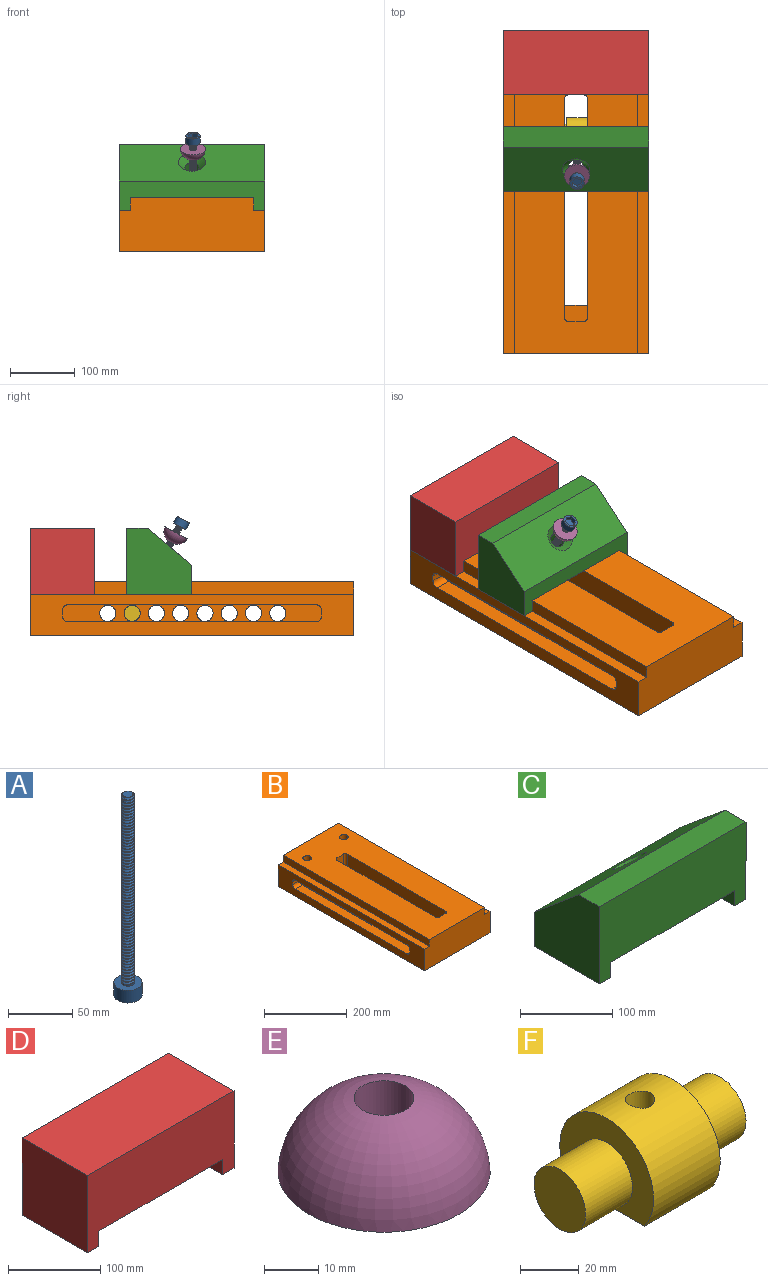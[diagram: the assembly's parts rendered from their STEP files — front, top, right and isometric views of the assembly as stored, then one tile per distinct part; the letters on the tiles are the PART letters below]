
ASSEMBLY  parts=6 mates=5
PART A: 17 faces, bbox 22x22x193.4 mm
  f0: cylinder r=5.25mm len=179mm, axis (0,0,-1), area -432.2mm2, adj f2,f5,f13,f15,f16
  f1: plane 8.52x8.52mm, normal (0,0,1), area 56mm2, adj f2,f14,f15,f16
  f2: cone r=4.25mm half-angle=45deg, axis (0,0,-1), area 19.5mm2, adj f0,f1,f14,f15
  f3: plane 22x22mm, normal (0,0,-1), area 184.4mm2, adj f4,f6,f7,f8,f9,f10,f11
  f4: cylinder r=11mm len=22mm, axis (0,0,1), area 829.4mm2, adj f3,f5
  f5: plane 22x22mm, normal (0,0,1), area 293.5mm2, adj f0,f4
  f6: plane 8.68x8mm, normal (0,1,0), area 69.4mm2, adj f3,f7,f11,f12
  f7: plane 8x7.52mm, normal (0.87,0.5,0), area 69.4mm2, adj f3,f6,f8,f12
  f8: plane 8x7.52mm, normal (0.87,-0.5,0), area 69.4mm2, adj f3,f7,f9,f12
  f9: plane 8.68x8mm, normal (0,-1,0), area 69.4mm2, adj f3,f8,f10,f12
  f10: plane 8x7.52mm, normal (-0.87,-0.5,0), area 69.4mm2, adj f3,f9,f11,f12
  f11: plane 8x7.52mm, normal (-0.87,0.5,0), area 69.4mm2, adj f3,f6,f10,f12
  f12: plane 17.36x15.04mm, normal (0,0,-1), area 195.8mm2, adj f6,f7,f8,f9,f10,f11
  f13: plane 2.39x1.3mm, normal (0,1,0.08), area 1.6mm2, adj f0,f15,f16
  f14: plane 1.1x1.01mm, normal (0,-1,-0.08), area 0mm2, adj f1,f2,f16
  f15: bspline ~180.19x12.12mm, area 3301.9mm2, adj f0,f1,f2,f13,f16
  f16: bspline ~180.2x12.12mm, area 3336.6mm2, adj f0,f1,f13,f14,f15
PART B: 84 faces, bbox 225x500x83.9 mm
  f0: plane 22.5x12.64mm, normal (0,0,-1), area 284.3mm2, adj f31,f40,f81,f83
  f1: plane 22.5x12.64mm, normal (0,0,-1), area 284.3mm2, adj f27,f36,f80,f82
  f2: plane 80x32.57mm, normal (0,0,-1), area 2340.6mm2, adj f27,f31,f32,f33,f34,f36,f37,f38
  f3: plane 22.5x12.64mm, normal (0,0,-1), area 284.3mm2, adj f31,f40,f79,f81
  f4: plane 22.5x12.64mm, normal (0,0,-1), area 284.3mm2, adj f27,f36,f78,f80
  f5: plane 22.5x12.64mm, normal (0,0,-1), area 284.3mm2, adj f31,f40,f77,f79
  f6: plane 22.5x12.64mm, normal (0,0,-1), area 284.3mm2, adj f27,f36,f76,f78
  f7: plane 22.5x12.64mm, normal (0,0,-1), area 284.3mm2, adj f31,f40,f75,f77
  f8: plane 22.5x12.64mm, normal (0,0,-1), area 284.3mm2, adj f27,f36,f74,f76
  f9: plane 22.5x12.64mm, normal (0,0,-1), area 284.3mm2, adj f31,f40,f73,f75
  f10: plane 22.5x12.64mm, normal (0,0,-1), area 284.3mm2, adj f27,f36,f72,f74
  f11: plane 22.5x12.64mm, normal (0,0,-1), area 284.3mm2, adj f31,f40,f71,f73
  f12: plane 22.5x12.64mm, normal (0,0,-1), area 284.3mm2, adj f27,f36,f70,f72
  f13: plane 22.5x12.64mm, normal (0,0,-1), area 284.3mm2, adj f31,f40,f69,f71
  f14: plane 22.5x12.64mm, normal (0,0,-1), area 284.3mm2, adj f27,f36,f68,f70
  f15: plane 30.08x22.5mm, normal (0,0,-1), area 669.1mm2, adj f29,f30,f31,f40,f69
  f16: plane 30.08x22.5mm, normal (0,0,-1), area 669.1mm2, adj f27,f28,f29,f36,f68
  f17: plane 500x225mm, normal (0,0,-1), area 83000.9mm2, adj f18,f19,f25,f26,f27,f28,f29,f30
  f18: plane 500x63.9mm, normal (-1,0,0), area 21459.5mm2, adj f17,f24,f25,f26,f47,f48,f49,f50
  f19: plane 500x63.9mm, normal (1,0,0), area 21459.5mm2, adj f17,f20,f25,f26,f59,f60,f61,f62
  f20: plane 500x17.5mm, normal (0,0,1), area 8750mm2, adj f19,f21,f25,f26
  f21: plane 500x20mm, normal (1,0,0), area 10000mm2, adj f20,f22,f25,f26
  f22: plane 500x190mm, normal (0,0,1), area 82094.8mm2, adj f21,f23,f25,f26,f36,f37,f38,f39
  f23: plane 500x20mm, normal (-1,0,0), area 10000mm2, adj f22,f24,f25,f26
  f24: plane 500x17.5mm, normal (0,0,1), area 8750mm2, adj f18,f23,f25,f26
  f25: plane 225x83.9mm, normal (0,-1,0), area 18177.5mm2, adj f17,f18,f19,f20,f21,f22,f23,f24
  f26: plane 225x83.9mm, normal (0,1,0), area 18177.5mm2, adj f17,f18,f19,f20,f21,f22,f23,f24
  f27: plane 338.01x36mm, normal (-1,0,0), area 9945.4mm2, adj f1,f2,f4,f6,f8,f10,f12,f14
  f28: cylinder r=6mm len=36mm, axis (0,0,-1), area 339.3mm2, adj f16,f17,f27,f29
  f29: plane 68x36mm, normal (0,1,0), area 2448mm2, adj f15,f16,f17,f28,f30,f35
  f30: cylinder r=6mm len=36mm, axis (0,0,-1), area 339.3mm2, adj f15,f17,f29,f31
  f31: plane 338.01x36mm, normal (1,0,0), area 9945.4mm2, adj f0,f2,f3,f5,f7,f9,f11,f13
  f32: cylinder r=6mm len=36mm, axis (0,0,-1), area 339.3mm2, adj f2,f17,f31,f33
  f33: plane 68x36mm, normal (0,-1,0), area 2448mm2, adj f2,f17,f32,f34
  f34: cylinder r=6mm len=36mm, axis (0,0,-1), area 339.3mm2, adj f2,f17,f27,f33
  f35: plane 35x24.99mm, normal (0,0,1), area 859.2mm2, adj f29,f36,f40,f41,f42,f43
  f36: plane 338x47.9mm, normal (-1,0,0), area 14486.2mm2, adj f1,f2,f4,f6,f8,f10,f12,f14
  f37: cylinder r=6mm len=47.9mm, axis (0,0,1), area 451.4mm2, adj f2,f22,f36,f38
  f38: plane 47.9x23mm, normal (0,-1,0), area 1101.7mm2, adj f2,f22,f37,f39
  f39: cylinder r=6mm len=47.9mm, axis (0,0,1), area 451.4mm2, adj f2,f22,f38,f40
  f40: plane 338x47.9mm, normal (1,0,0), area 14486.2mm2, adj f0,f2,f3,f5,f7,f9,f11,f13
  f41: cylinder r=6mm len=47.9mm, axis (0,0,1), area 451.4mm2, adj f22,f35,f40,f42
  f42: plane 47.9x23mm, normal (0,1,0), area 1101.7mm2, adj f22,f35,f41,f43
  f43: cylinder r=6mm len=47.9mm, axis (0,0,1), area 451.4mm2, adj f22,f35,f36,f42
  f44: cylinder r=10.45mm len=62.9mm, axis (0,0,-1), area 4130mm2, adj f22,f45
  f45: plane 31.2x31.2mm, normal (0,0,-1), area 421.5mm2, adj f44,f46
  f46: cylinder r=15.6mm len=31.2mm, axis (0,0,-1), area 2058.4mm2, adj f17,f45
  f47: plane 25x8.4mm, normal (0,1,0), area 210mm2, adj f18,f48,f54,f55
  f48: cylinder r=9mm len=25mm, axis (-1,0,0), area 353.4mm2, adj f18,f47,f49,f55
  f49: plane 382x25mm, normal (0,0,-1), area 9550mm2, adj f18,f48,f50,f55
  f50: cylinder r=9mm len=25mm, axis (-1,0,0), area 353.4mm2, adj f18,f49,f51,f55
  f51: plane 25x8.4mm, normal (0,-1,0), area 210mm2, adj f18,f50,f52,f55
  f52: cylinder r=9mm len=25mm, axis (-1,0,0), area 353.4mm2, adj f18,f51,f53,f55
  f53: plane 382x25mm, normal (0,0,1), area 9550mm2, adj f18,f52,f54,f55
  f54: cylinder r=9mm len=25mm, axis (-1,0,0), area 353.4mm2, adj f18,f47,f53,f55
  f55: plane 400x26.4mm, normal (-1,0,0), area 6563.5mm2, adj f47,f48,f49,f50,f51,f52,f53,f54
  f56: cylinder r=15.6mm len=31.2mm, axis (0,0,-1), area 2058.4mm2, adj f17,f57
  f57: plane 31.2x31.2mm, normal (0,0,-1), area 421.5mm2, adj f56,f58
  f58: cylinder r=10.45mm len=62.9mm, axis (0,0,-1), area 4130mm2, adj f22,f57
  f59: plane 25x8.4mm, normal (0,1,0), area 210mm2, adj f19,f60,f66,f67
  f60: cylinder r=9mm len=25mm, axis (1,0,0), area 353.4mm2, adj f19,f59,f61,f67
  f61: plane 382x25mm, normal (0,0,-1), area 9550mm2, adj f19,f60,f62,f67
  f62: cylinder r=9mm len=25mm, axis (1,0,0), area 353.4mm2, adj f19,f61,f63,f67
  f63: plane 25x8.4mm, normal (0,-1,0), area 210mm2, adj f19,f62,f64,f67
  f64: cylinder r=9mm len=25mm, axis (1,0,0), area 353.4mm2, adj f19,f63,f65,f67
  f65: plane 382x25mm, normal (0,0,1), area 9550mm2, adj f19,f64,f66,f67
  f66: cylinder r=9mm len=25mm, axis (1,0,0), area 353.4mm2, adj f19,f59,f65,f67
  f67: plane 400x26.4mm, normal (1,0,0), area 6563.5mm2, adj f59,f60,f61,f62,f63,f64,f65,f66
  f68: cylinder r=12.5mm len=70mm, axis (-1,0,0), area 4555.6mm2, adj f14,f16,f27,f36,f67
  f69: cylinder r=12.5mm len=70mm, axis (-1,0,0), area 4555.6mm2, adj f13,f15,f31,f40,f55
  f70: cylinder r=12.5mm len=70mm, axis (-1,0,0), area 4555.6mm2, adj f12,f14,f27,f36,f67
  f71: cylinder r=12.5mm len=70mm, axis (-1,0,0), area 4555.6mm2, adj f11,f13,f31,f40,f55
  f72: cylinder r=12.5mm len=70mm, axis (-1,0,0), area 4555.6mm2, adj f10,f12,f27,f36,f67
  f73: cylinder r=12.5mm len=70mm, axis (-1,0,0), area 4555.6mm2, adj f9,f11,f31,f40,f55
  f74: cylinder r=12.5mm len=70mm, axis (-1,0,0), area 4555.6mm2, adj f8,f10,f27,f36,f67
  f75: cylinder r=12.5mm len=70mm, axis (-1,0,0), area 4555.6mm2, adj f7,f9,f31,f40,f55
  f76: cylinder r=12.5mm len=70mm, axis (-1,0,0), area 4555.6mm2, adj f6,f8,f27,f36,f67
  f77: cylinder r=12.5mm len=70mm, axis (-1,0,0), area 4555.6mm2, adj f5,f7,f31,f40,f55
  f78: cylinder r=12.5mm len=70mm, axis (-1,0,0), area 4555.6mm2, adj f4,f6,f27,f36,f67
  f79: cylinder r=12.5mm len=70mm, axis (-1,0,0), area 4555.6mm2, adj f3,f5,f31,f40,f55
  f80: cylinder r=12.5mm len=70mm, axis (-1,0,0), area 4555.6mm2, adj f1,f4,f27,f36,f67
  f81: cylinder r=12.5mm len=70mm, axis (-1,0,0), area 4555.6mm2, adj f0,f3,f31,f40,f55
  f82: cylinder r=12.5mm len=70mm, axis (-1,0,0), area 4555.6mm2, adj f1,f2,f27,f36,f67
  f83: cylinder r=12.5mm len=70mm, axis (-1,0,0), area 4555.6mm2, adj f0,f2,f31,f40,f55
PART C: 18 faces, bbox 225.1x100.1x102.6 mm
  f0: cylinder r=11mm len=65.95mm, axis (0,0.64,0.77), area 2312.6mm2, adj f1,f12,f13,f14,f16,f17
  f1: cone r=11mm half-angle=45deg, axis (0,0.64,0.77), area 1419.8mm2, adj f0,f6,f14,f15,f16
  f2: plane 100x17.5mm, normal (0,0,-1), area 1750mm2, adj f3,f5,f9,f10
  f3: plane 225x102.5mm, normal (0,-1,0), area 19262.5mm2, adj f2,f4,f7,f8,f9,f10,f11,f12
  f4: plane 100x17.5mm, normal (0,0,-1), area 1750mm2, adj f3,f5,f8,f11
  f5: plane 225x45.39mm, normal (0,1,0), area 6413mm2, adj f2,f4,f6,f8,f9,f10,f11,f12
  f6: plane 225x68mm, normal (0,0.64,0.77), area 18594.6mm2, adj f1,f5,f7,f8,f9
  f7: plane 225x32mm, normal (0,0,1), area 7200mm2, adj f3,f6,f8,f9
  f8: plane 102.5x100mm, normal (1,0,0), area 8308.3mm2, adj f3,f4,f5,f6,f7
  f9: plane 102.5x100mm, normal (-1,0,0), area 8308.3mm2, adj f2,f3,f5,f6,f7
  f10: plane 100x20mm, normal (1,0,0), area 2000mm2, adj f2,f3,f5,f12
  f11: plane 100x20mm, normal (-1,0,0), area 2000mm2, adj f3,f4,f5,f12
  f12: plane 190x100mm, normal (0,0,-1), area 17752.7mm2, adj f0,f3,f5,f10,f11,f13,f14,f15
  f13: plane 44.49x37.36mm, normal (1,0,0), area 831.2mm2, adj f0,f12,f14
  f14: cylinder r=10mm len=44.49mm, axis (0,0,-1), area 651mm2, adj f0,f1,f12,f13,f15
  f15: plane 39.32x2.07mm, normal (0,-1,0), area 78.5mm2, adj f1,f12,f14,f16
  f16: cylinder r=10mm len=44.49mm, axis (0,0,-1), area 651mm2, adj f0,f1,f12,f15,f17
  f17: plane 44.49x37.36mm, normal (-1,0,0), area 831.2mm2, adj f0,f12,f16
PART D: 14 faces, bbox 225x100x102.5 mm
  f0: plane 102.5x100mm, normal (-1,0,0), area 10250mm2, adj f1,f7,f8,f9
  f1: plane 100x17.5mm, normal (0,0,-1), area 1750mm2, adj f0,f2,f8,f9
  f2: plane 100x20mm, normal (1,0,0), area 2000mm2, adj f1,f3,f8,f9
  f3: plane 190x100mm, normal (0,0,-1), area 18842.9mm2, adj f2,f4,f8,f9,f11,f13
  f4: plane 100x20mm, normal (-1,0,0), area 2000mm2, adj f3,f5,f8,f9
  f5: plane 100x17.5mm, normal (0,0,-1), area 1750mm2, adj f4,f6,f8,f9
  f6: plane 102.5x100mm, normal (1,0,0), area 10250mm2, adj f5,f7,f8,f9
  f7: plane 225x100mm, normal (0,0,1), area 22500mm2, adj f0,f6,f8,f9
  f8: plane 225x102.5mm, normal (0,-1,0), area 19262.5mm2, adj f0,f1,f2,f3,f4,f5,f6,f7
  f9: plane 225x102.5mm, normal (0,1,0), area 19262.5mm2, adj f0,f1,f2,f3,f4,f5,f6,f7
  f10: cone r=0mm half-angle=59deg, axis (0,0,-1), area 91.6mm2, adj f11
  f11: cylinder r=5mm len=75mm, axis (0,0,-1), area 2356.2mm2, adj f3,f10
  f12: cone r=0mm half-angle=59deg, axis (0,0,-1), area 91.6mm2, adj f13
  f13: cylinder r=5mm len=75mm, axis (0,0,-1), area 2356.2mm2, adj f3,f12
PART E: 3 faces, bbox 39x39x16.4 mm
  f0: torus R=1.21mm, axis (0,0,-1), area 2064.7mm2, adj f1,f2
  f1: plane 39x39mm, normal (0,0,-1), area 1099.6mm2, adj f0,f2
  f2: cylinder r=5.5mm len=16.39mm, axis (0,0,-1), area 566.4mm2, adj f0,f1
PART F: 9 faces, bbox 77x45x35.9 mm
  f0: plane 45x35.9mm, normal (1,0,0), area 877.3mm2, adj f2,f3,f8
  f1: plane 45x35.9mm, normal (-1,0,0), area 877.3mm2, adj f2,f6,f8
  f2: cylinder r=22.5mm len=45mm, axis (-1,0,0), area 3101.4mm2, adj f0,f1,f7,f8
  f3: cylinder r=12.4mm len=24.8mm, axis (-1,0,0), area 1753mm2, adj f0,f4
  f4: plane 24.8x24.8mm, normal (1,0,0), area 483.1mm2, adj f3
  f5: plane 24.8x24.8mm, normal (-1,0,0), area 483.1mm2, adj f6
  f6: cylinder r=12.4mm len=24.8mm, axis (-1,0,0), area 1753mm2, adj f1,f5
  f7: cylinder r=5mm len=35.9mm, axis (0,0,1), area 1119mm2, adj f2,f8
  f8: plane 36.15x32mm, normal (0,0,-1), area 1078.2mm2, adj f0,f1,f2,f7
PLACE A rot(axis=(-0.28,0.93,0.24),171.7deg) t=(114,-230.78,168.83)mm
PLACE B at identity fixed
PLACE C rot(axis=(0,0,1),180deg) t=(225,-149,63.9)mm
PLACE D t=(0,0,166.4)mm
PLACE E rot(axis=(-0.88,0.47,0.12),154.8deg) t=(114,-225.3,158.81)mm
PLACE F rot(axis=(1,0,0),28.6deg) t=(114,-157.5,34.7)mm
MATE slider C.f3 <-> D.f8  axis (0,1,0) through (225,-149,63.9)mm
MATE revolute F.f3 <-> B.f80  axis (-1,0,0) through (130,-157.5,34.7)mm
MATE cylindrical A.f0 <-> F.f7  axis (0,0.48,-0.88) through (114,-144.48,10.87)mm
MATE slider E.f0 <-> A.f4  axis (0,-0.48,0.88) through (114,-225.3,158.81)mm
MATE fastened D.f5 <-> B.f20  axis (0,0,1) through (225,0,63.9)mm
